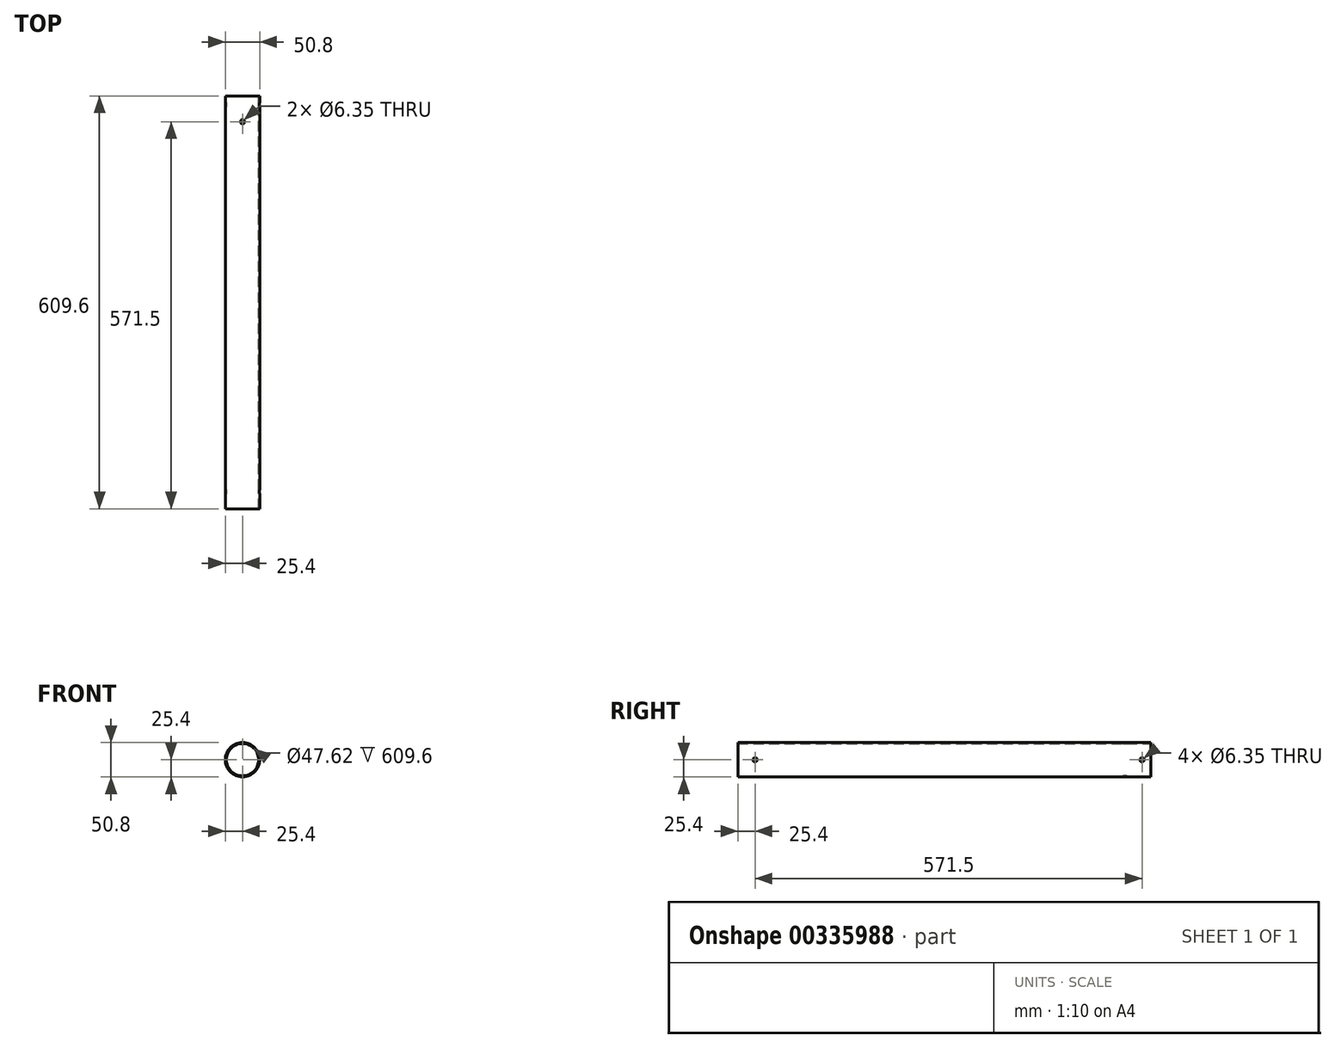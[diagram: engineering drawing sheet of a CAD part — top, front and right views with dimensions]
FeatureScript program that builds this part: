
annotation { "Feature Type Name" : "Feature", "Feature Type Description" : "" }
export const myFeature = defineFeature(function(context is Context, id is Id, definition is map)
    precondition{}
    {
        {
            var Q0;
            Q0=qCreatedBy(makeId("Front.planeOp"),FACE);
            var sketch = newSketch(context, id + "F0", { "sketchPlane" : qUnion([Q0])});
            skCircle(sketch, "E0", {"center": v(0, 0) * mm, "radius": 23.81 * mm});
            skCircle(sketch, "E1", {"center": v(0, 0) * mm, "radius": 25.4 * mm});
            skSolve(sketch);
        }
        {
            var Q0;
            Q0=makeQuery(id+"F0.imprint","IMPRINT",FACE,{"disambiguationData":[TD([[makeQuery(id+"F0.imprint","IMPRINT",EDGE,{"derivedFrom":sQuery(id+"F0.wireOp",EDGE,"E0")}),-1.0]])]});
            extrude(context, id + "F1", {"entities" : qUnion([Q0]), "endBound" : BoundingType.SYMMETRIC, "depth" : 609.6 * mm});
        }
        {
            var Q0;
            Q0=qCreatedBy(makeId("Right.planeOp"),FACE);
            var sketch = newSketch(context, id + "F2", { "sketchPlane" : qUnion([Q0])});
            skPoint(sketch, "E2", {"position": v(-279.4, 0) * mm});
            skPoint(sketch, "E3", {"position": v(292.1, 0) * mm});
            skCircle(sketch, "E4", {"center": v(-279.4, 0) * mm, "radius": 3.17 * mm});
            skCircle(sketch, "E5", {"center": v(292.1, 0) * mm, "radius": 3.18 * mm});
            skSolve(sketch);
        }
        {
            var Q0;
            Q0=makeQuery(id+"F2.imprint","IMPRINT",FACE,{"disambiguationData":[TD([[makeQuery(id+"F2.imprint","IMPRINT",EDGE,{"derivedFrom":sQuery(id+"F2.wireOp",EDGE,"E4")}),1.0]])]});
            var Q1;
            Q1=makeQuery(id+"F2.imprint","IMPRINT",FACE,{"disambiguationData":[TD([[makeQuery(id+"F2.imprint","IMPRINT",EDGE,{"derivedFrom":sQuery(id+"F2.wireOp",EDGE,"E5")}),1.0]])]});
            extrude(context, id + "F3", {"entities" : qUnion([Q0, Q1]), "operationType" : NewBodyOperationType.REMOVE, "endBound" : BoundingType.SYMMETRIC, "oppositeDirection" : true, "depth" : 50.8 * mm});
        }
        {
            var Q0;
            Q0=qCreatedBy(makeId("Top.planeOp"),FACE);
            var sketch = newSketch(context, id + "F4", { "sketchPlane" : qUnion([Q0])});
            skPoint(sketch, "E6", {"position": v(0, 266.7) * mm});
            skCircle(sketch, "E7", {"center": v(0, 266.7) * mm, "radius": 3.18 * mm});
            skSolve(sketch);
        }
        {
            var Q0;
            Q0=makeQuery(id+"F4.imprint","IMPRINT",FACE,{"disambiguationData":[TD([[makeQuery(id+"F4.imprint","IMPRINT",EDGE,{"derivedFrom":sQuery(id+"F4.wireOp",EDGE,"E7")}),1.0]])]});
            extrude(context, id + "F5", {"entities" : qUnion([Q0]), "operationType" : NewBodyOperationType.REMOVE, "endBound" : BoundingType.SYMMETRIC, "oppositeDirection" : true, "depth" : 50.8 * mm});
        }
    });
